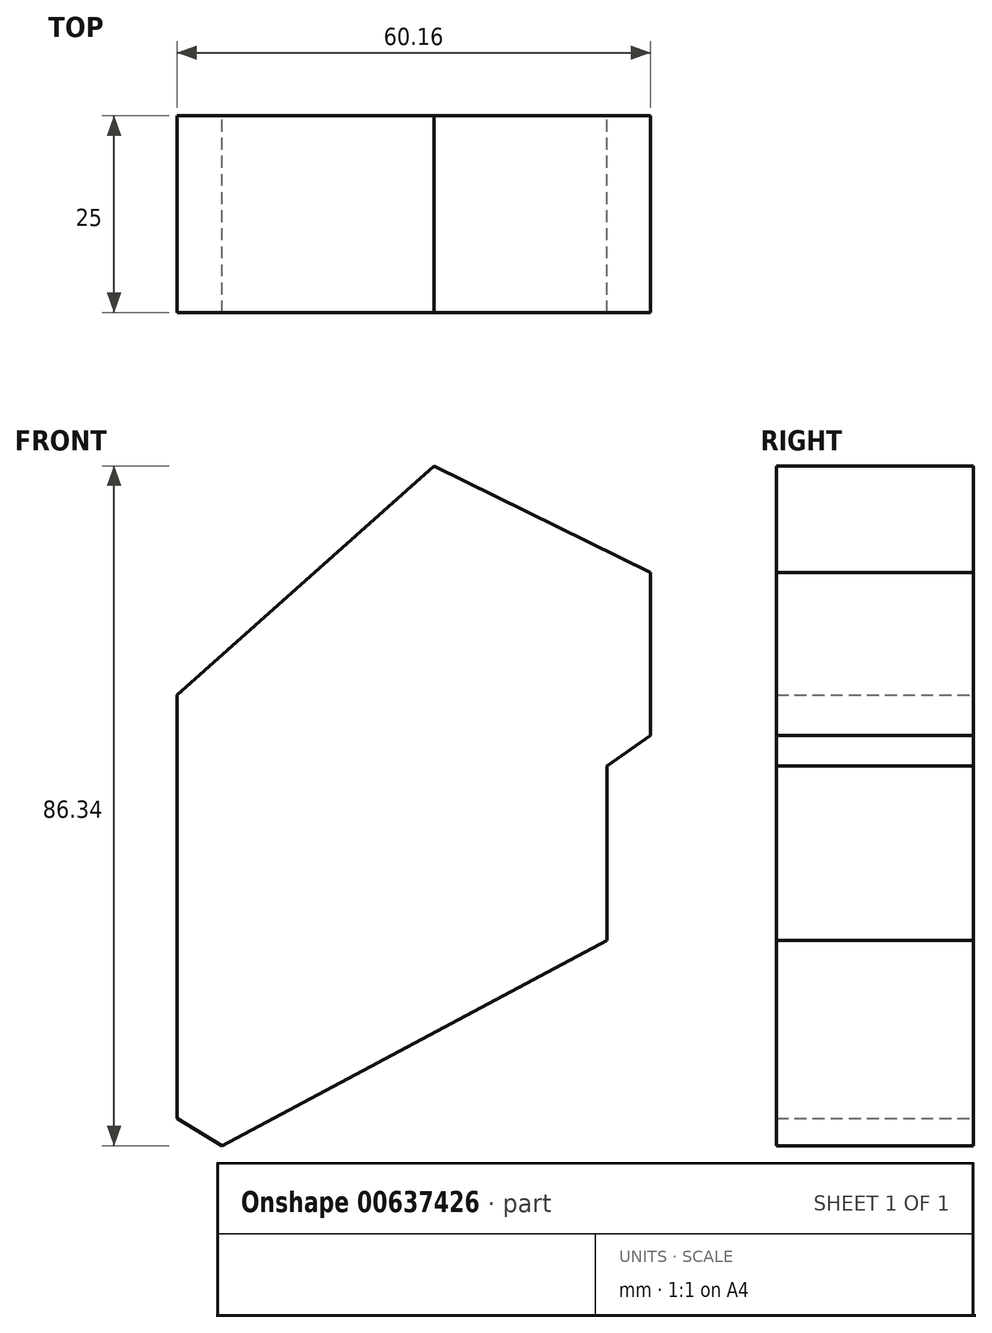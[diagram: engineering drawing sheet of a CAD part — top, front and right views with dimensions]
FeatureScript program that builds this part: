
annotation { "Feature Type Name" : "Feature", "Feature Type Description" : "" }
export const myFeature = defineFeature(function(context is Context, id is Id, definition is map)
    precondition{}
    {
        {
            var Q0;
            Q0=qCreatedBy(makeId("Front.planeOp"),FACE);
            var sketch = newSketch(context, id + "F0", { "sketchPlane" : qUnion([Q0])});
            skLineSegment(sketch, "E0", {"start": v(-32.67, 19.14) * mm, "end": v(-32.67, -34.68) * mm});
            skLineSegment(sketch, "E1", {"start": v(-32.67, -34.68) * mm, "end": v(-26.9, -38.13) * mm});
            skLineSegment(sketch, "E2", {"start": v(-26.9, -38.13) * mm, "end": v(-26.9, 10.22) * mm});
            skLineSegment(sketch, "E3", {"start": v(-26.9, 10.22) * mm, "end": v(-13.38, 6.19) * mm});
            skLineSegment(sketch, "E4", {"start": v(-13.38, 6.19) * mm, "end": v(-13.38, -7.34) * mm});
            skLineSegment(sketch, "E5", {"start": v(-13.38, -7.34) * mm, "end": v(-3.02, -7.34) * mm});
            skLineSegment(sketch, "E6", {"start": v(-3.02, -7.34) * mm, "end": v(-3.02, 10.22) * mm});
            skLineSegment(sketch, "E7", {"start": v(-3.02, 10.22) * mm, "end": v(27.49, 34.68) * mm});
            skLineSegment(sketch, "E8", {"start": v(27.49, 34.68) * mm, "end": v(0, 48.2) * mm});
            skLineSegment(sketch, "E9", {"start": v(0, 48.2) * mm, "end": v(-32.67, 19.14) * mm});
            skLineSegment(sketch, "E10", {"start": v(27.49, 34.68) * mm, "end": v(27.49, 13.96) * mm});
            skLineSegment(sketch, "E11", {"start": v(27.49, 13.96) * mm, "end": v(-3.02, -7.34) * mm});
            skLineSegment(sketch, "E12", {"start": v(-26.9, -38.13) * mm, "end": v(21.95, -12.04) * mm});
            skLineSegment(sketch, "E13", {"start": v(21.95, -12.04) * mm, "end": v(21.95, 10.1) * mm});
            skSolve(sketch);
        }
        {
            var Q0;
            Q0 = qSketchRegion(id + "F0", true);
            extrude(context, id + "F1", {"entities" : qUnion([Q0]), "depth" : 25 * mm, "offsetDistance" : 25 * mm});
        }
    });
